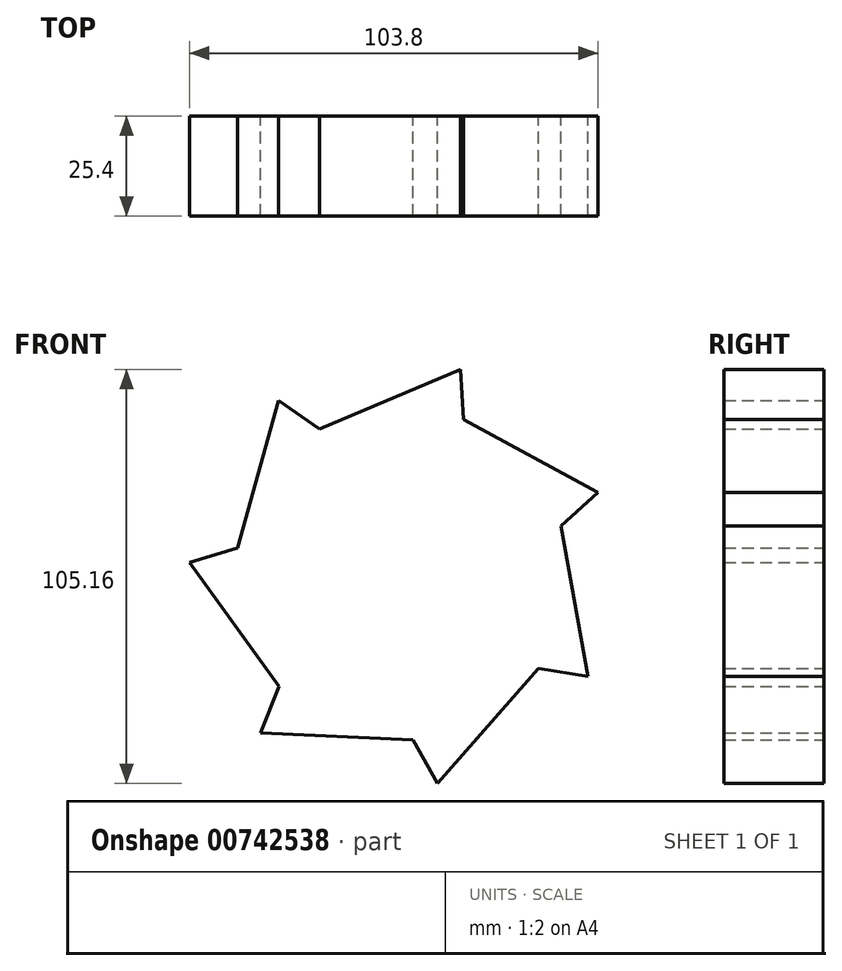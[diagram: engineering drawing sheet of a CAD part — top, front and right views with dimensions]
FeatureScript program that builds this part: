
annotation { "Feature Type Name" : "Feature", "Feature Type Description" : "" }
export const myFeature = defineFeature(function(context is Context, id is Id, definition is map)
    precondition{}
    {
        {
            var Q0;
            Q0=qCreatedBy(makeId("Front.planeOp"),FACE);
            var sketch = newSketch(context, id + "F0", { "sketchPlane" : qUnion([Q0])});
            skCircle(sketch, "E0.cCircle", {"center": v(-29.95, 30.7) * mm, "radius": 38.1 * mm, "construction": true});
            skLineSegment(sketch, "E0.0", {"start": v(10.55, 42.88) * mm, "end": v(4.82, 6.64) * mm});
            skLineSegment(sketch, "E0.1", {"start": v(4.82, 6.64) * mm, "end": v(-27.09, -11.49) * mm});
            skLineSegment(sketch, "E0.2", {"start": v(-27.09, -11.49) * mm, "end": v(-61.15, 2.16) * mm});
            skLineSegment(sketch, "E0.3", {"start": v(-61.15, 2.16) * mm, "end": v(-71.72, 37.3) * mm});
            skLineSegment(sketch, "E0.4", {"start": v(-71.72, 37.3) * mm, "end": v(-50.83, 67.47) * mm});
            skLineSegment(sketch, "E0.5", {"start": v(-50.83, 67.47) * mm, "end": v(-14.22, 69.96) * mm});
            skLineSegment(sketch, "E0.6", {"start": v(-14.22, 69.96) * mm, "end": v(10.55, 42.88) * mm});
            skPoint(sketch, "E0.0.midPoint", {"position": v(7.69, 24.76) * mm});
            skLineSegment(sketch, "E1", {"start": v(-71.72, 37.3) * mm, "end": v(-83.88, 33.64) * mm});
            skLineSegment(sketch, "E2", {"start": v(-83.88, 33.64) * mm, "end": v(-61.15, 2.16) * mm});
            skLineSegment(sketch, "E3", {"start": v(-71.72, 37.3) * mm, "end": v(-61.28, 74.7) * mm});
            skPoint(sketch, "E3.endSnap0", {"position": v(-61.28, 52.39) * mm});
            skLineSegment(sketch, "E4", {"start": v(-61.28, 74.7) * mm, "end": v(-50.83, 67.47) * mm});
            skLineSegment(sketch, "E5", {"start": v(-50.83, 67.47) * mm, "end": v(-15.08, 82.63) * mm});
            skLineSegment(sketch, "E6", {"start": v(-15.08, 82.63) * mm, "end": v(-14.22, 69.96) * mm});
            skLineSegment(sketch, "E7", {"start": v(10.55, 42.88) * mm, "end": v(19.92, 51.46) * mm});
            skLineSegment(sketch, "E8", {"start": v(19.92, 51.46) * mm, "end": v(-14.22, 69.96) * mm});
            skLineSegment(sketch, "E9", {"start": v(10.55, 42.88) * mm, "end": v(17.37, 4.65) * mm});
            skLineSegment(sketch, "E10", {"start": v(17.37, 4.65) * mm, "end": v(4.82, 6.64) * mm});
            skLineSegment(sketch, "E11", {"start": v(-27.09, -11.49) * mm, "end": v(-20.81, -22.53) * mm});
            skLineSegment(sketch, "E12", {"start": v(-20.81, -22.53) * mm, "end": v(4.82, 6.64) * mm});
            skLineSegment(sketch, "E13", {"start": v(-61.15, 2.16) * mm, "end": v(-65.87, -9.63) * mm});
            skPoint(sketch, "E13.endSnap0", {"position": v(-44.12, -4.66) * mm});
            skLineSegment(sketch, "E14", {"start": v(-65.87, -9.63) * mm, "end": v(-27.09, -11.49) * mm});
            skSolve(sketch);
        }
        {
            var Q0;
            Q0=makeQuery(id+"F0.imprint","IMPRINT",FACE,{"disambiguationData":[TD([[makeQuery(id+"F0.imprint","IMPRINT",EDGE,{"derivedFrom":sQuery(id+"F0.wireOp",EDGE,"E0.0")}),1.0]])]});
            var Q1;
            Q1=makeQuery(id+"F0.imprint","IMPRINT",FACE,{"disambiguationData":[TD([[makeQuery(id+"F0.imprint","IMPRINT",EDGE,{"derivedFrom":sQuery(id+"F0.wireOp",EDGE,"E0.1")}),1.0]])]});
            var Q2;
            Q2=makeQuery(id+"F0.imprint","IMPRINT",FACE,{"disambiguationData":[TD([[makeQuery(id+"F0.imprint","IMPRINT",EDGE,{"derivedFrom":sQuery(id+"F0.wireOp",EDGE,"E0.2")}),1.0]])]});
            var Q3;
            Q3=makeQuery(id+"F0.imprint","IMPRINT",FACE,{"disambiguationData":[TD([[makeQuery(id+"F0.imprint","IMPRINT",EDGE,{"derivedFrom":sQuery(id+"F0.wireOp",EDGE,"E0.3")}),1.0]])]});
            var Q4;
            Q4=makeQuery(id+"F0.imprint","IMPRINT",FACE,{"disambiguationData":[TD([[makeQuery(id+"F0.imprint","IMPRINT",EDGE,{"derivedFrom":sQuery(id+"F0.wireOp",EDGE,"E0.4")}),1.0]])]});
            var Q5;
            Q5=makeQuery(id+"F0.imprint","IMPRINT",FACE,{"disambiguationData":[TD([[makeQuery(id+"F0.imprint","IMPRINT",EDGE,{"derivedFrom":sQuery(id+"F0.wireOp",EDGE,"E0.5")}),1.0]])]});
            var Q6;
            Q6=makeQuery(id+"F0.imprint","IMPRINT",FACE,{"disambiguationData":[TD([[makeQuery(id+"F0.imprint","IMPRINT",EDGE,{"derivedFrom":sQuery(id+"F0.wireOp",EDGE,"E0.6")}),1.0]])]});
            var Q7;
            Q7=makeQuery(id+"F0.imprint","IMPRINT",FACE,{"disambiguationData":[TD([[makeQuery(id+"F0.imprint","IMPRINT",EDGE,{"derivedFrom":sQuery(id+"F0.wireOp",EDGE,"E0.0")}),-1.0]])]});
            extrude(context, id + "F1", {"entities" : qUnion([Q0, Q1, Q2, Q3, Q4, Q5, Q6, Q7]), "depth" : 25.4 * mm, "offsetDistance" : 25.4 * mm});
        }
    });
